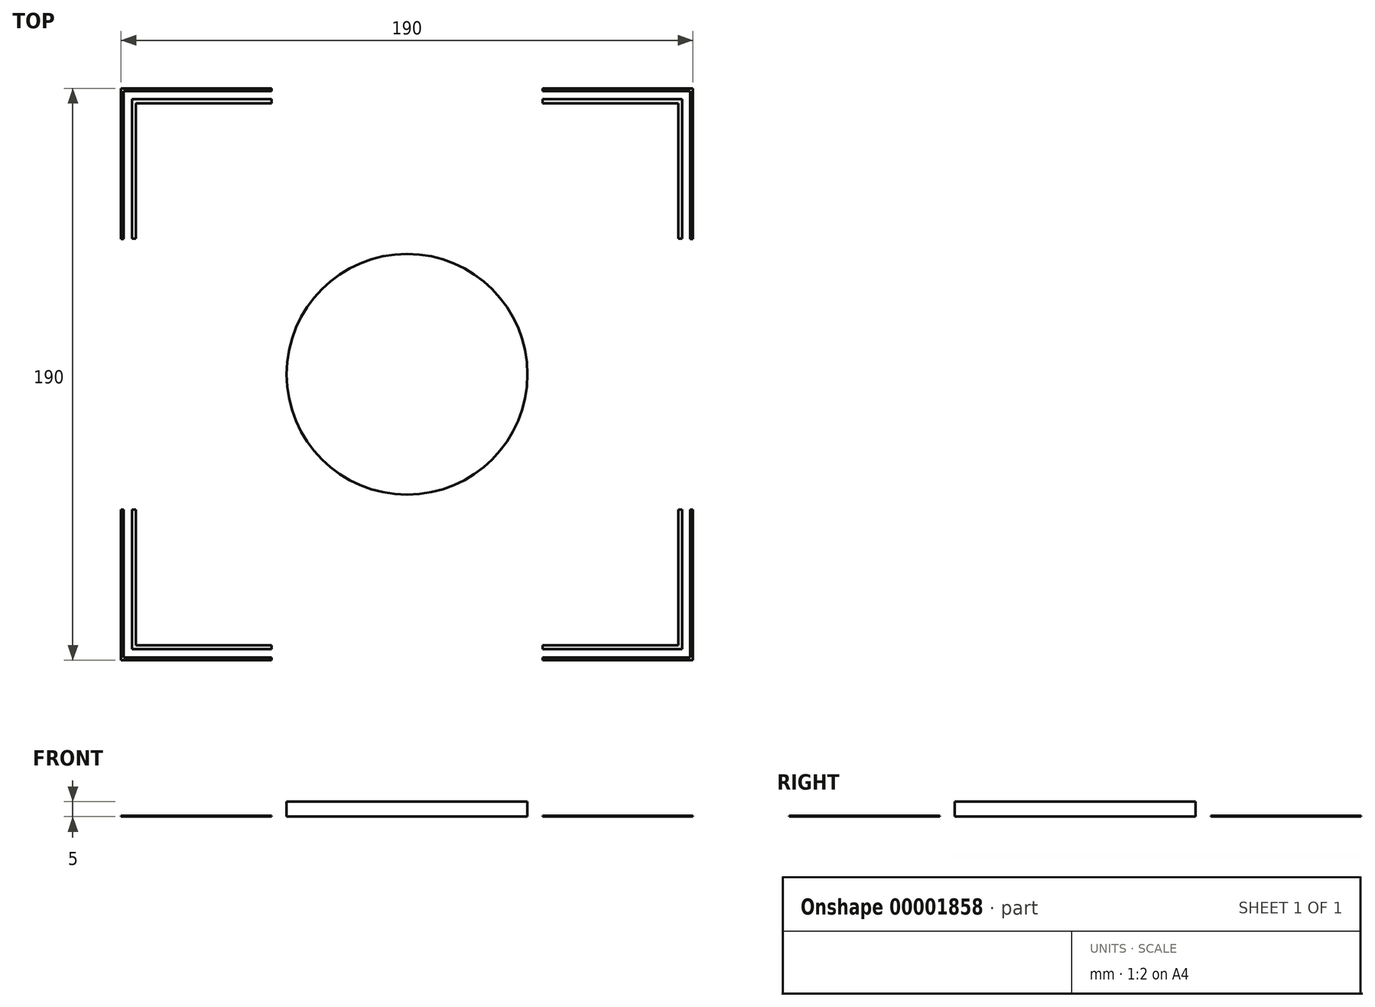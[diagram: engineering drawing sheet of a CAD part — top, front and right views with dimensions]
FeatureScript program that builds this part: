
annotation { "Feature Type Name" : "Feature", "Feature Type Description" : "" }
export const myFeature = defineFeature(function(context is Context, id is Id, definition is map)
    precondition{}
    {
        {
            var Q0;
            Q0=qCreatedBy(makeId("Top.planeOp"),FACE);
            var sketch = newSketch(context, id + "F0", { "sketchPlane" : qUnion([Q0])});
            skLineSegment(sketch, "E0.bottom", {"start": v(-95, -95) * mm, "end": v(-45, -95) * mm});
            skLineSegment(sketch, "E0.top", {"start": v(-95, -45) * mm, "end": v(-94.1, -45) * mm});
            skLineSegment(sketch, "E0.left", {"start": v(-95, -95) * mm, "end": v(-95, -45) * mm});
            skLineSegment(sketch, "E0.right", {"start": v(-45, -95) * mm, "end": v(-45, -94.1) * mm});
            skLineSegment(sketch, "E1.top", {"start": v(-45, -94.1) * mm, "end": v(-94.1, -94.1) * mm});
            skLineSegment(sketch, "E1.right", {"start": v(-94.1, -45) * mm, "end": v(-94.1, -94.1) * mm});
            skLineSegment(sketch, "E2", {"start": v(0, 0) * mm, "end": v(-94.1, -94.1) * mm, "construction": true});
            skLineSegment(sketch, "E3.bottom", {"start": v(-91.37, -91.37) * mm, "end": v(-45.02, -91.37) * mm});
            skLineSegment(sketch, "E3.top", {"start": v(-91.37, -45.02) * mm, "end": v(-90.07, -45.02) * mm});
            skLineSegment(sketch, "E3.left", {"start": v(-91.37, -91.37) * mm, "end": v(-91.37, -45.02) * mm});
            skLineSegment(sketch, "E3.right", {"start": v(-45.02, -91.37) * mm, "end": v(-45.02, -90.07) * mm});
            skLineSegment(sketch, "E4.top", {"start": v(-45.02, -90.07) * mm, "end": v(-90.07, -90.07) * mm});
            skLineSegment(sketch, "E4.right", {"start": v(-90.07, -45.02) * mm, "end": v(-90.07, -90.07) * mm});
            skCircle(sketch, "E5", {"center": v(0, 0) * mm, "radius": 25 * mm});
            skLineSegment(sketch, "E6.0.MirrorCS", {"start": v(-45, 95) * mm, "end": v(-45, 94.1) * mm});
            skLineSegment(sketch, "E6.1.MirrorCS", {"start": v(-95, 45) * mm, "end": v(-94.1, 45) * mm});
            skLineSegment(sketch, "E6.2.MirrorCS", {"start": v(-45.02, 91.37) * mm, "end": v(-45.02, 90.07) * mm});
            skLineSegment(sketch, "E6.3.MirrorCS", {"start": v(-91.37, 45.02) * mm, "end": v(-90.07, 45.02) * mm});
            skLineSegment(sketch, "E6.4.MirrorCS", {"start": v(-95, 95) * mm, "end": v(-95, 45) * mm});
            skLineSegment(sketch, "E6.5.MirrorCS", {"start": v(-45.02, 90.07) * mm, "end": v(-90.07, 90.07) * mm});
            skLineSegment(sketch, "E6.6.MirrorCS", {"start": v(-91.37, 91.37) * mm, "end": v(-91.37, 45.02) * mm});
            skLineSegment(sketch, "E6.7.MirrorCS", {"start": v(-95, 95) * mm, "end": v(-45, 95) * mm});
            skLineSegment(sketch, "E6.8.MirrorCS", {"start": v(-91.37, 91.37) * mm, "end": v(-45.02, 91.37) * mm});
            skLineSegment(sketch, "E6.9.MirrorCS", {"start": v(-90.07, 45.02) * mm, "end": v(-90.07, 90.07) * mm});
            skLineSegment(sketch, "E6.10.MirrorCS", {"start": v(-45, 94.1) * mm, "end": v(-94.1, 94.1) * mm});
            skLineSegment(sketch, "E6.11.MirrorCS", {"start": v(-94.1, 45) * mm, "end": v(-94.1, 94.1) * mm});
            skLineSegment(sketch, "E7.0.MirrorCS", {"start": v(45, -95) * mm, "end": v(45, -94.1) * mm});
            skLineSegment(sketch, "E7.1.MirrorCS", {"start": v(45.02, -91.37) * mm, "end": v(45.02, -90.07) * mm});
            skLineSegment(sketch, "E7.2.MirrorCS", {"start": v(91.37, -45.02) * mm, "end": v(90.07, -45.02) * mm});
            skLineSegment(sketch, "E7.3.MirrorCS", {"start": v(95, -45) * mm, "end": v(94.1, -45) * mm});
            skLineSegment(sketch, "E7.4.MirrorCS", {"start": v(45, 95) * mm, "end": v(45, 94.1) * mm});
            skLineSegment(sketch, "E7.5.MirrorCS", {"start": v(91.37, 45.02) * mm, "end": v(90.07, 45.02) * mm});
            skLineSegment(sketch, "E7.6.MirrorCS", {"start": v(45.02, 91.37) * mm, "end": v(45.02, 90.07) * mm});
            skLineSegment(sketch, "E7.7.MirrorCS", {"start": v(95, 45) * mm, "end": v(94.1, 45) * mm});
            skLineSegment(sketch, "E7.8.MirrorCS", {"start": v(91.37, -91.37) * mm, "end": v(91.37, -45.02) * mm});
            skLineSegment(sketch, "E7.9.MirrorCS", {"start": v(94.1, 45) * mm, "end": v(94.1, 94.1) * mm});
            skLineSegment(sketch, "E7.10.MirrorCS", {"start": v(45, 94.1) * mm, "end": v(94.1, 94.1) * mm});
            skLineSegment(sketch, "E7.11.MirrorCS", {"start": v(90.07, -45.02) * mm, "end": v(90.07, -90.07) * mm});
            skLineSegment(sketch, "E7.12.MirrorCS", {"start": v(91.37, -91.37) * mm, "end": v(45.02, -91.37) * mm});
            skLineSegment(sketch, "E7.13.MirrorCS", {"start": v(91.37, 91.37) * mm, "end": v(91.37, 45.02) * mm});
            skLineSegment(sketch, "E7.14.MirrorCS", {"start": v(95, 95) * mm, "end": v(45, 95) * mm});
            skLineSegment(sketch, "E7.15.MirrorCS", {"start": v(95, -95) * mm, "end": v(95, -45) * mm});
            skLineSegment(sketch, "E7.16.MirrorCS", {"start": v(95, 95) * mm, "end": v(95, 45) * mm});
            skLineSegment(sketch, "E7.17.MirrorCS", {"start": v(95, -95) * mm, "end": v(45, -95) * mm});
            skLineSegment(sketch, "E7.18.MirrorCS", {"start": v(45.02, -90.07) * mm, "end": v(90.07, -90.07) * mm});
            skLineSegment(sketch, "E7.19.MirrorCS", {"start": v(90.07, 45.02) * mm, "end": v(90.07, 90.07) * mm});
            skLineSegment(sketch, "E7.20.MirrorCS", {"start": v(45.02, 90.07) * mm, "end": v(90.07, 90.07) * mm});
            skLineSegment(sketch, "E7.21.MirrorCS", {"start": v(94.1, -45) * mm, "end": v(94.1, -94.1) * mm});
            skLineSegment(sketch, "E7.22.MirrorCS", {"start": v(91.37, 91.37) * mm, "end": v(45.02, 91.37) * mm});
            skLineSegment(sketch, "E7.23.MirrorCS", {"start": v(45, -94.1) * mm, "end": v(94.1, -94.1) * mm});
            skSolve(sketch);
        }
        {
            var Q0;
            Q0=makeQuery(id+"F0.imprint","IMPRINT",FACE,{"disambiguationData":[TD([[makeQuery(id+"F0.imprint","IMPRINT",EDGE,{"derivedFrom":sQuery(id+"F0.wireOp",EDGE,"E0.bottom")}),1.0]])]});
            var Q1;
            Q1=makeQuery(id+"F0.imprint","IMPRINT",FACE,{"disambiguationData":[TD([[makeQuery(id+"F0.imprint","IMPRINT",EDGE,{"derivedFrom":sQuery(id+"F0.wireOp",EDGE,"E3.bottom")}),1.0]])]});
            var Q2;
            Q2=makeQuery(id+"F0.imprint","IMPRINT",FACE,{"disambiguationData":[TD([[makeQuery(id+"F0.imprint","IMPRINT",EDGE,{"derivedFrom":sQuery(id+"F0.wireOp",EDGE,"E6.0.MirrorCS")}),-1.0]])]});
            var Q3;
            Q3=makeQuery(id+"F0.imprint","IMPRINT",FACE,{"disambiguationData":[TD([[makeQuery(id+"F0.imprint","IMPRINT",EDGE,{"derivedFrom":sQuery(id+"F0.wireOp",EDGE,"E6.2.MirrorCS")}),-1.0]])]});
            var Q4;
            Q4=makeQuery(id+"F0.imprint","IMPRINT",FACE,{"disambiguationData":[TD([[makeQuery(id+"F0.imprint","IMPRINT",EDGE,{"derivedFrom":sQuery(id+"F0.wireOp",EDGE,"E7.0.MirrorCS")}),-1.0]])]});
            var Q5;
            Q5=makeQuery(id+"F0.imprint","IMPRINT",FACE,{"disambiguationData":[TD([[makeQuery(id+"F0.imprint","IMPRINT",EDGE,{"derivedFrom":sQuery(id+"F0.wireOp",EDGE,"E7.1.MirrorCS")}),-1.0]])]});
            var Q6;
            Q6=makeQuery(id+"F0.imprint","IMPRINT",FACE,{"disambiguationData":[TD([[makeQuery(id+"F0.imprint","IMPRINT",EDGE,{"derivedFrom":sQuery(id+"F0.wireOp",EDGE,"E7.4.MirrorCS")}),1.0]])]});
            var Q7;
            Q7=makeQuery(id+"F0.imprint","IMPRINT",FACE,{"disambiguationData":[TD([[makeQuery(id+"F0.imprint","IMPRINT",EDGE,{"derivedFrom":sQuery(id+"F0.wireOp",EDGE,"E7.5.MirrorCS")}),-1.0]])]});
            extrude(context, id + "F1", {"entities" : qUnion([Q0, Q1, Q2, Q3, Q4, Q5, Q6, Q7]), "depth" : 0.3 * mm});
        }
        {
            var Q0;
            Q0=qCreatedBy(makeId("Top.planeOp"),FACE);
            var sketch = newSketch(context, id + "F2", { "sketchPlane" : qUnion([Q0])});
            skCircle(sketch, "E8", {"center": v(0, 0) * mm, "radius": 40 * mm});
            skSolve(sketch);
        }
        {
            var Q0;
            Q0=makeQuery(id+"F2.imprint","IMPRINT",FACE,{"disambiguationData":[TD([[makeQuery(id+"F2.imprint","IMPRINT",EDGE,{"derivedFrom":sQuery(id+"F2.wireOp",EDGE,"E8")}),1.0]])]});
            extrude(context, id + "F3", {"entities" : qUnion([Q0]), "depth" : 5 * mm});
        }
    });
